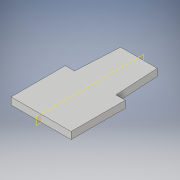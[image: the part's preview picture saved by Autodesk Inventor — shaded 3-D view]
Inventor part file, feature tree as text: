
AUTODESK INVENTOR PART (.ipt)
format: ipt  version: 2018 (Build 220112000, 112)  size: 101,376 bytes
history: native  units: in
note: dims shown in document units (in); Inventor stores cm internally (conversion verified against a paired STEP export)
features: extrude x1, plane x1, sketch x1
ambient origin geometry x8: Origin, YZ Plane, XZ Plane, XY Plane, X Axis, Y Axis, Z Axis, Center Point
bodies: Body1 (feature_tree)
feature tree (3):
  extrude  "Extrusion2"  Depth=0.2756in TaperAngle=0.0deg
  plane  "Work Plane1"
  sketch  "Sketch1"  dims[d4=3.8583in d5=0.2756in d6=0.0in d7=1.1811in]
